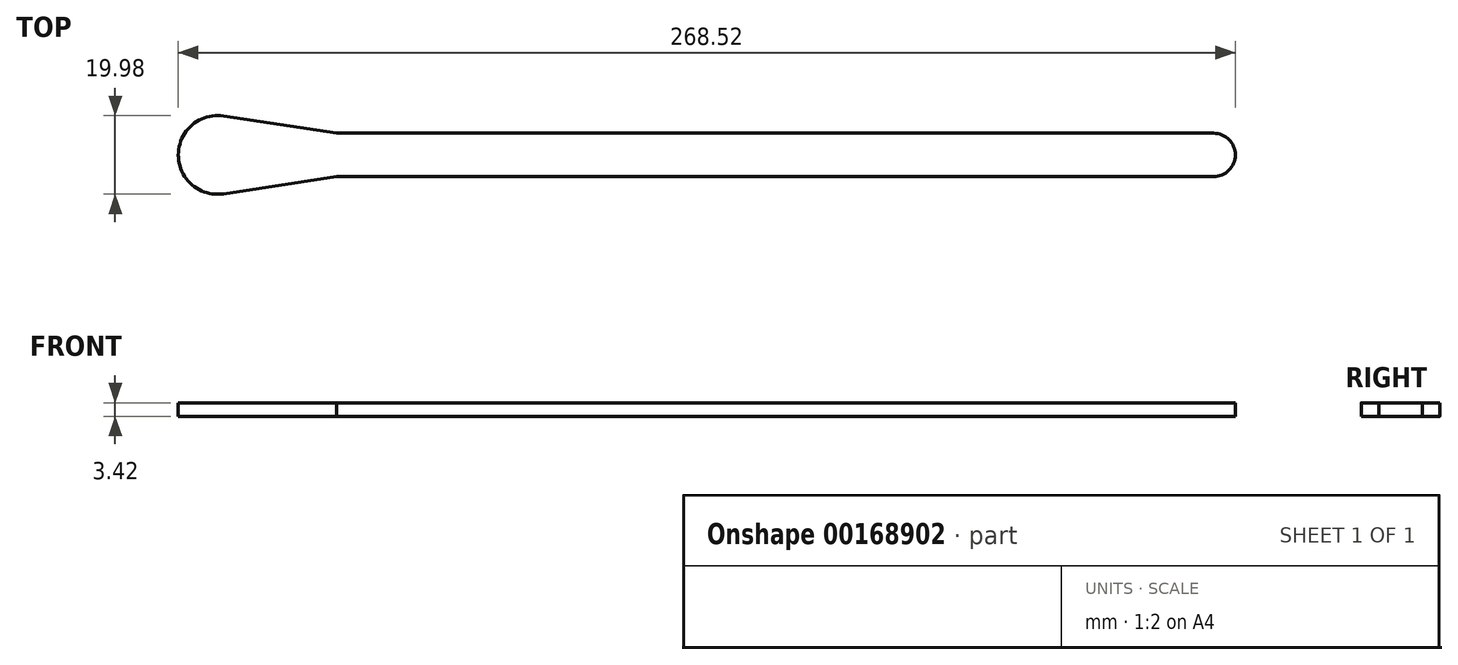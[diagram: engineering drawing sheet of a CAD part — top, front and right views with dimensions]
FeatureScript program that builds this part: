
annotation { "Feature Type Name" : "Feature", "Feature Type Description" : "" }
export const myFeature = defineFeature(function(context is Context, id is Id, definition is map)
    precondition{}
    {
        {
            var Q0;
            Q0=qCreatedBy(makeId("Top.planeOp"),FACE);
            var sketch = newSketch(context, id + "F0", { "sketchPlane" : qUnion([Q0])});
            skArc(sketch, "E0", {"start": v(1.5, 9.88) * mm, "mid": v(-10, 0) * mm, "end": v(1.5, -9.88) * mm});
            skLineSegment(sketch, "E1", {"start": v(253.02, 5.51) * mm, "end": v(30.23, 5.51) * mm});
            skLineSegment(sketch, "E2", {"start": v(253.02, -5.51) * mm, "end": v(30.23, -5.51) * mm});
            skLineSegment(sketch, "E3", {"start": v(1.5, 9.88) * mm, "end": v(30.23, 5.51) * mm});
            skLineSegment(sketch, "E4", {"start": v(1.5, -9.88) * mm, "end": v(30.23, -5.51) * mm});
            skArc(sketch, "E5", {"start": v(253.02, -5.51) * mm, "mid": v(258.53, 0) * mm, "end": v(253.02, 5.51) * mm});
            skSolve(sketch);
        }
        {
            var Q0;
            Q0=makeQuery(id+"F0.imprint","IMPRINT",FACE,{"disambiguationData":[TD([[makeQuery(id+"F0.imprint","IMPRINT",EDGE,{"derivedFrom":sQuery(id+"F0.wireOp",EDGE,"E0")}),1.0]])]});
            extrude(context, id + "F1", {"entities" : qUnion([Q0]), "depth" : 3.42 * mm});
        }
    });
